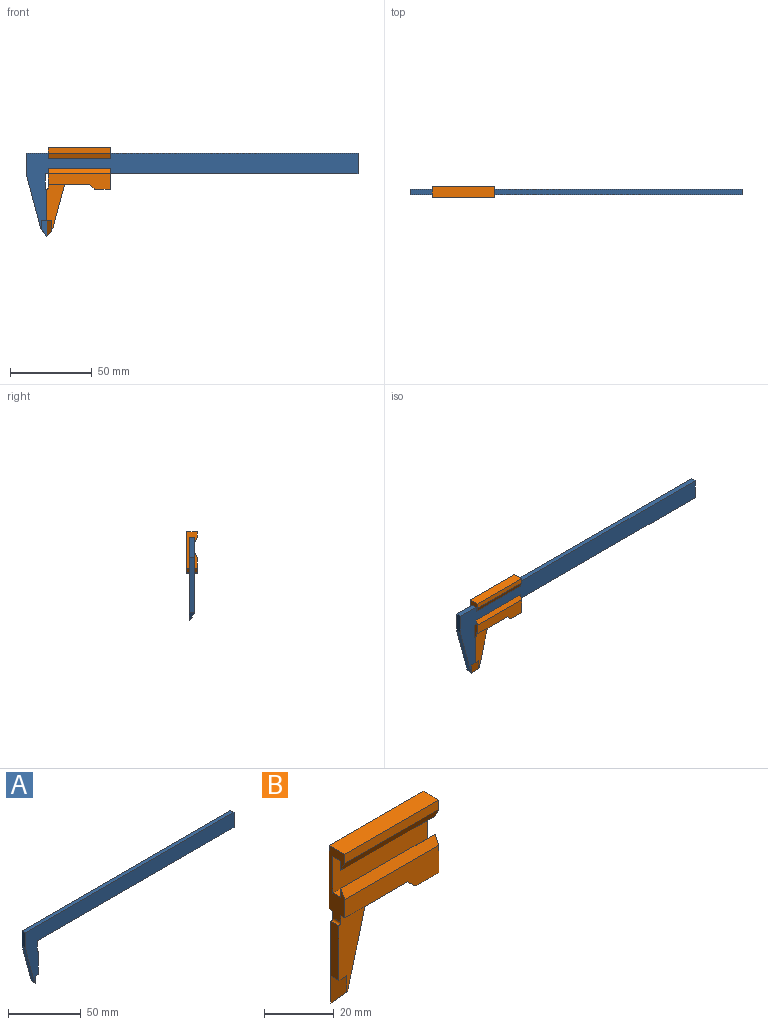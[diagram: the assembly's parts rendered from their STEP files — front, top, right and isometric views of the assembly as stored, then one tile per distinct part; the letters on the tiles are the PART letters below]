
ASSEMBLY  parts=2 mates=1
PART A: 13 faces, bbox 203.2x3.2x50.8 mm
  f0: plane 203.2x50.8mm, normal (0,1,0), area 2857.2mm2, adj f2,f3,f4,f5,f6,f7,f8,f9
  f1: plane 3.18x3.18mm, normal (0,0,-1), area 5mm2, adj f9,f11,f12
  f2: plane 8.74x3.18mm, normal (1,0,0), area 27.7mm2, adj f0,f3,f10,f11
  f3: plane 191.29x3.18mm, normal (0,0,-1), area 607.3mm2, adj f0,f2,f4,f11
  f4: plane 12.7x3.18mm, normal (1,0,0), area 40.3mm2, adj f0,f3,f5,f11
  f5: plane 203.2x3.18mm, normal (0,0,1), area 645.2mm2, adj f0,f4,f6,f11
  f6: plane 12.7x3.18mm, normal (-1,0,0), area 40.3mm2, adj f0,f5,f7,f11
  f7: plane 33.74x9.04mm, normal (-0.97,0,-0.26), area 110.9mm2, adj f0,f6,f8,f11
  f8: plane 4.36x3.66mm, normal (-0.77,0,-0.64), area 10.2mm2, adj f0,f7,f11,f12
  f9: plane 19.05x3.18mm, normal (1,0,0), area 60.5mm2, adj f0,f1,f10,f11
  f10: cylinder r=0.79mm len=3.18mm, axis (0,1,0), area 3.9mm2, adj f0,f2,f9,f11
  f11: plane 203.2x47.02mm, normal (0,-1,0), area 2833mm2, adj f1,f2,f3,f4,f5,f6,f7,f8
  f12: plane 9.53x3.18mm, normal (0.71,-0.71,0), area 34.3mm2, adj f0,f1,f8,f11
PART B: 25 faces, bbox 38.9x6.4x54 mm
  f0: plane 31.75x11mm, normal (0,1,0), area 206.3mm2, adj f1,f3,f4,f5,f6,f7,f10
  f1: plane 9.53x3.18mm, normal (-0.71,-0.71,0), area 34.3mm2, adj f0,f2,f3,f24
  f2: plane 3.18x3.18mm, normal (0,0,-1), area 5mm2, adj f1,f4,f24
  f3: plane 4.36x3.66mm, normal (0.77,0,-0.64), area 10.2mm2, adj f0,f1,f5,f24
  f4: plane 19.05x3.18mm, normal (-1,0,0), area 60.5mm2, adj f0,f2,f7,f24
  f5: plane 27.39x7.34mm, normal (0.97,0,-0.26), area 90mm2, adj f0,f3,f10,f24
  f6: plane 24.61x6.35mm, normal (-1,0,0), area 93.3mm2, adj f0,f7,f9,f10,f13,f14,f15,f16
  f7: cylinder r=0.79mm len=3.18mm, axis (0,1,0), area 3.9mm2, adj f0,f4,f6,f24
  f8: plane 25.4x6.35mm, normal (1,0,0), area 105.8mm2, adj f9,f12,f13,f14,f15,f16,f17,f18
  f9: plane 38.1x3.18mm, normal (0,-1,0), area 121mm2, adj f6,f8,f13,f21
  f10: plane 25.4x6.35mm, normal (0,0,-1), area 128.9mm2, adj f0,f5,f6,f11,f14,f15,f24
  f11: plane 6.35x2.8mm, normal (-0.71,0,-0.71), area 25.2mm2, adj f10,f14,f15,f23
  f12: plane 9x6.35mm, normal (0,0,-1), area 57.1mm2, adj f8,f14,f15,f23
  f13: plane 38.1x6.35mm, normal (0,0,1), area 241.9mm2, adj f6,f8,f9,f15
  f14: plane 38.1x9.53mm, normal (0,-1,0), area 277.2mm2, adj f6,f8,f10,f11,f12,f22,f23
  f15: plane 38.1x25.4mm, normal (0,1,0), area 882mm2, adj f6,f8,f10,f11,f12,f13,f23
  f16: plane 38.1x3.18mm, normal (0,1,0), area 121mm2, adj f6,f8,f17,f22
  f17: plane 38.1x3.18mm, normal (0,0,1), area 121mm2, adj f6,f8,f16,f18
  f18: plane 38.1x12.7mm, normal (0,-1,0), area 483.9mm2, adj f6,f8,f17,f19
  f19: plane 38.1x3.18mm, normal (0,0,-1), area 121mm2, adj f6,f8,f18,f20
  f20: plane 38.1x3.18mm, normal (0,1,0), area 121mm2, adj f6,f8,f19,f21
  f21: plane 38.1x3.18mm, normal (0,-0.89,-0.45), area 135.2mm2, adj f6,f8,f9,f20
  f22: plane 38.1x3.18mm, normal (0,-0.89,0.45), area 135.2mm2, adj f6,f8,f14,f16
  f23: cylinder r=1.27mm len=6.35mm, axis (0,1,0), area 6.3mm2, adj f11,f12,f14,f15
  f24: plane 27.97x11mm, normal (0,-1,0), area 182.1mm2, adj f1,f2,f3,f4,f5,f6,f7,f10
PLACE A t=(-14.63,-10.98,12.82)mm fixed
PLACE B t=(-83.69,-9.4,11.24)mm
MATE slider B.f6 <-> A.f4  axis (-1,0,0) through (-102.74,-10.98,19.17)mm
